# Revit family: CVL-CM
name_source: partatom
category: Lighting Fixtures
revit_build: Autodesk Revit 2014 (Build: 20130308_1515(x64)
units: mm (PartAtom-declared; Revit-internal decimal feet)

## types (6) — shared parameters
Assembly Code = D5020200
Color Filter = 16777215
Default Elevation = 48"
Description = Parabolic louver combines with curved shape for
direct/indirect distribution
Dimming Lamp Color Temperature Shift = <None>
Emit Shape Visible in Rendering = No
Emit from Rectangle Length = 46"
Emit from Rectangle Width = 7"
Glass = Hubbell - White Glass
Housing Material = Hubbell - White
Lamp = T5, T5HO, T8
Load Classification = Lighting
Manufacturer = Alera Lighting
Model = CVL
Photometric Notes = More IES files download on Photometric Web Link
Photometric Web Link = https://www.hubbell.com
Power Factor = 1
Product Documentation Link = https://hubbellcdn.com
Product Page URL = https://www.hubbell.com
Row Length = 48"
Tilt Angle = -90.00°
URL = https://www.hubbell.com
Voltage = 120 V

## per-type parameters (varying)
| type | Apparent Load | Distribution | Lamp Type | Photometric Web File | Suspension Height | Watts |
| CVL-1T5HO-0/100-LS-EP | 59 VA | 0% Uplight, 100% Downlight | One T5HO Lamp | CVL-1T5HO-0 100-LS-EP.ies | 48" | 59 W |
| CVL-1T5HO-85/15-LD-EP | 62 VA | 85% Uplight, 15% Downlight | One T5HO Lamp | CVL-1T5HO-85 15-LD-EP.ies | 48" | 62 W |
| CVL-2T5HO-20/80-LD-EP | 104 VA | 20% Uplight, 80% Downlight | Two T5HO Lamp | CVL-2T5HO-20 80-LD-EP.ies | 48" | 104 W |
| CVL-2T5HO-40/60-LS-EP | 115 VA | 40% Uplight, 60% Downlight | Two T5HO Lamp | CVL-2T5HO-40 60-LS-EP.ies | 48" | 115 W |
| CVL-3T5HO-0/100-LS-EP | 152 VA | 0% Uplight, 100% Downlight | Three T5HO Lamp | CVL-3T5HO-0 100-LS-EP.ies | 48" | 152 W |
| CVL-3T5HO-85/15-LS-EP | 185 VA | 85% Uplight, 15% Downlight | Three T5HO Lamp | CVL-3T5HO-85 15-LS-EP.ies | 36" | 185 W |

## geometry (parser evidence)
native form markers: Blend x5, Sweep x3
no freeform markers — native parametric forms only
